FCSTD DOCUMENT  (FreeCAD 0.20R29603 (Git))
Label: box_resonant_mode
License: All rights reserved
LicenseURL: http://en.wikipedia.org/wiki/All_rights_reserved
objects: App::DocumentObjectGroup×2, Part::Part2DObjectPython×1, Part::FeaturePython×1
note: 2 computed .brp shape members not serialized (recipe doc carries the construction recipe); baked Part::Feature solids carry a one-line shape summary decoded from their .brp

FEATURE [Part::Part2DObjectPython] Rectangle001  label="vacuum"  # Draft 2D object (typed FeaturePython)
  Area = 1e+06
  ChamferSize = 0
  Columns = 1
  FilletRadius = 0
  Height = 1000
  Length = 1000
  MakeFace = true
  Rows = 1
FEATURE [App::DocumentObjectGroup] Group001  label="regions"
  Group = -> [Rectangle001]
FEATURE [Part::FeaturePython] Rectangle001_child0  label="outer_boundary"  # WARN: FeaturePython — macro-defined, semantics opaque (R4)
  Base = -> Rectangle001
  FilterType = 1
  Invert = false
  OverrideMaxVal = 0
  WindowFrom = 80
  WindowTo = 100
  items = 0
FEATURE [App::DocumentObjectGroup] Group  label="boundaries"
  Group = -> [Rectangle001_child0]
